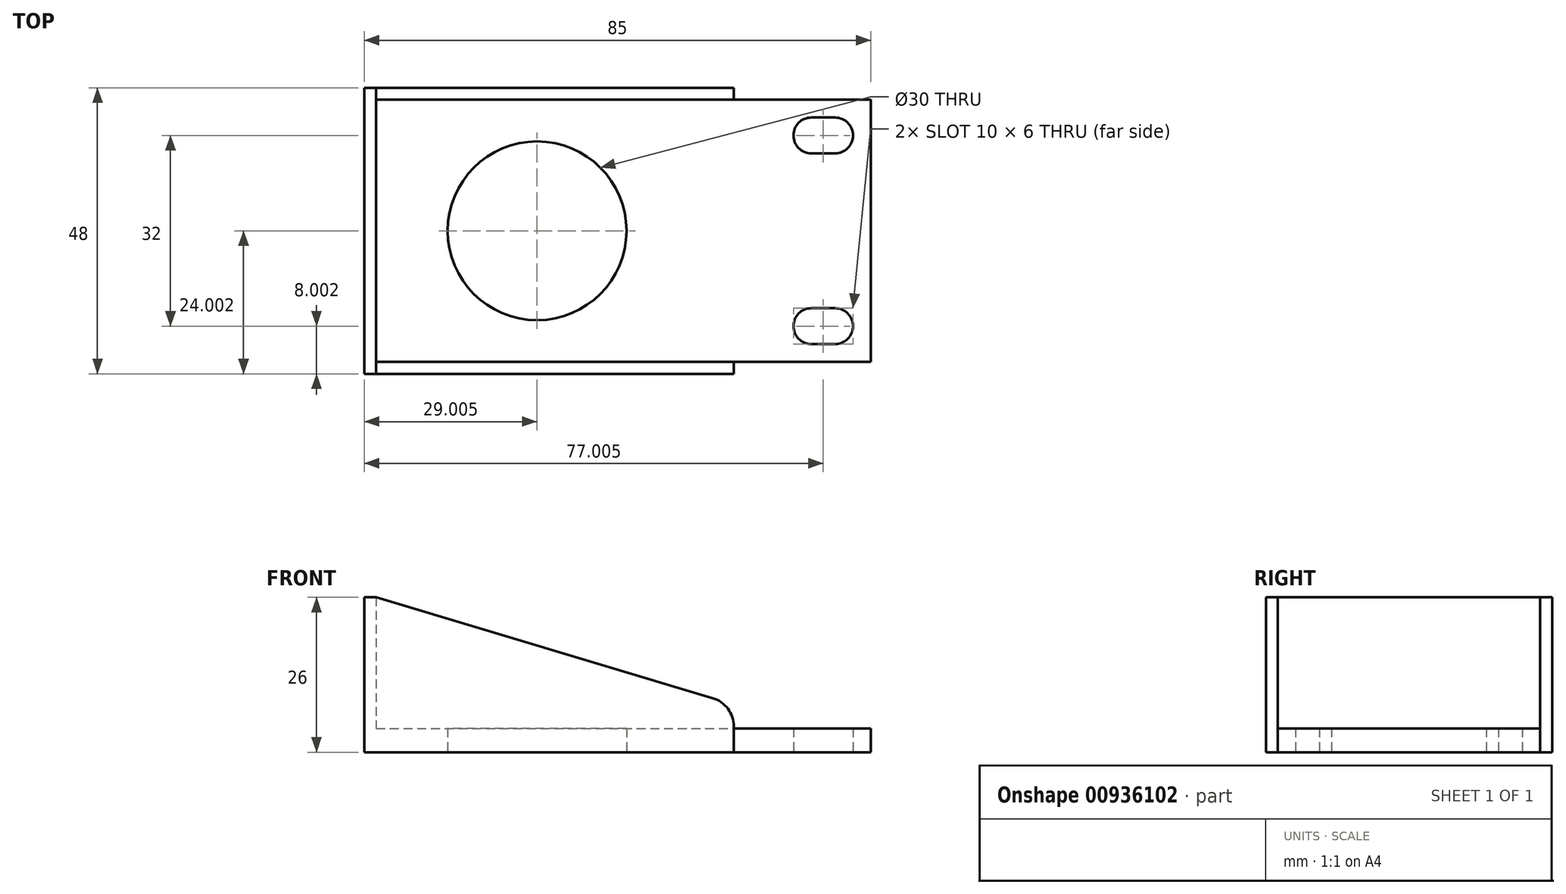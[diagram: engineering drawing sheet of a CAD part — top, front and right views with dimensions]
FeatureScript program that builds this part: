
annotation { "Feature Type Name" : "Feature", "Feature Type Description" : "" }
export const myFeature = defineFeature(function(context is Context, id is Id, definition is map)
    precondition{}
    {
        {
            var Q0;
            Q0=qCreatedBy(makeId("Top.planeOp"),FACE);
            var sketch = newSketch(context, id + "F0", { "sketchPlane" : qUnion([Q0])});
            skLineSegment(sketch, "E0.bottom", {"start": v(-33.04, 51.41) * mm, "end": v(43.96, 51.41) * mm});
            skLineSegment(sketch, "E0.top", {"start": v(-33.04, 7.41) * mm, "end": v(43.96, 7.41) * mm});
            skLineSegment(sketch, "E0.left", {"start": v(-33.04, 51.41) * mm, "end": v(-33.04, 7.41) * mm});
            skLineSegment(sketch, "E0.right", {"start": v(43.96, 51.41) * mm, "end": v(43.96, 7.41) * mm});
            skCircle(sketch, "E1", {"center": v(37.96, 13.41) * mm, "radius": 3 * mm});
            skCircle(sketch, "E2", {"center": v(37.96, 45.41) * mm, "radius": 3 * mm});
            skCircle(sketch, "E3", {"center": v(33.96, 45.41) * mm, "radius": 3 * mm});
            skCircle(sketch, "E4", {"center": v(33.96, 13.41) * mm, "radius": 3 * mm});
            skLineSegment(sketch, "E5", {"start": v(37.96, 48.41) * mm, "end": v(33.96, 48.41) * mm});
            skLineSegment(sketch, "E6", {"start": v(33.96, 42.41) * mm, "end": v(37.96, 42.41) * mm});
            skLineSegment(sketch, "E7", {"start": v(37.96, 10.41) * mm, "end": v(33.96, 10.41) * mm});
            skLineSegment(sketch, "E8", {"start": v(33.96, 16.41) * mm, "end": v(37.96, 16.41) * mm});
            skCircle(sketch, "E9", {"center": v(-12.04, 29.41) * mm, "radius": 15 * mm});
            skSolve(sketch);
        }
        {
            var Q0;
            Q0=makeQuery(id+"F0.imprint","IMPRINT",FACE,{"disambiguationData":[TD([[makeQuery(id+"F0.imprint","IMPRINT",EDGE,{"derivedFrom":sQuery(id+"F0.wireOp",EDGE,"E0.bottom")}),-1.0]])]});
            extrude(context, id + "F1", {"entities" : qUnion([Q0]), "depth" : 4 * mm, "offsetDistance" : 25 * mm});
        }
        {
            var Q0;
            Q0=makeQuery(id+"F1.opExtrude","CAP_FACE",FACE,{"disambiguationData":[OSD([sQuery(id+"F0.wireOp",EDGE,"E0.bottom"),sQuery(id+"F0.wireOp",EDGE,"E0.top"),sQuery(id+"F0.wireOp",EDGE,"E0.left"),sQuery(id+"F0.wireOp",EDGE,"E0.right"),sQuery(id+"F0.wireOp",EDGE,"E1"),sQuery(id+"F0.wireOp",EDGE,"E2"),sQuery(id+"F0.wireOp",EDGE,"E3"),sQuery(id+"F0.wireOp",EDGE,"E4"),sQuery(id+"F0.wireOp",EDGE,"E5"),sQuery(id+"F0.wireOp",EDGE,"E6"),sQuery(id+"F0.wireOp",EDGE,"E7"),sQuery(id+"F0.wireOp",EDGE,"E8"),sQuery(id+"F0.wireOp",EDGE,"E9")])],"isStart":false});
            var sketch = newSketch(context, id + "F2", { "sketchPlane" : qUnion([Q0])});
            skLineSegment(sketch, "E10.bottom", {"start": v(-33.04, 51.41) * mm, "end": v(20.96, 51.41) * mm});
            skLineSegment(sketch, "E10.top", {"start": v(-33.04, 53.41) * mm, "end": v(20.96, 53.41) * mm});
            skLineSegment(sketch, "E10.left", {"start": v(-33.04, 51.41) * mm, "end": v(-33.04, 53.41) * mm});
            skLineSegment(sketch, "E10.right", {"start": v(20.96, 51.41) * mm, "end": v(20.96, 53.41) * mm});
            skLineSegment(sketch, "E11.bottom", {"start": v(-33.04, 7.41) * mm, "end": v(20.96, 7.41) * mm});
            skLineSegment(sketch, "E11.top", {"start": v(-33.04, 5.41) * mm, "end": v(20.96, 5.41) * mm});
            skLineSegment(sketch, "E11.left", {"start": v(-33.04, 7.41) * mm, "end": v(-33.04, 5.41) * mm});
            skLineSegment(sketch, "E11.right", {"start": v(20.96, 7.41) * mm, "end": v(20.96, 5.41) * mm});
            skLineSegment(sketch, "E12.bottom", {"start": v(-33.04, 53.41) * mm, "end": v(-39.04, 53.41) * mm});
            skLineSegment(sketch, "E12.top", {"start": v(-33.04, 5.41) * mm, "end": v(-39.04, 5.41) * mm});
            skLineSegment(sketch, "E12.left", {"start": v(-33.04, 53.41) * mm, "end": v(-33.04, 5.41) * mm});
            skLineSegment(sketch, "E12.right", {"start": v(-39.04, 53.41) * mm, "end": v(-39.04, 5.41) * mm});
            skSolve(sketch);
        }
        {
            var Q0;
            {var subQ0=sQuery(id+"F2.wireOp",EDGE,"E10.bottom");Q0=makeQuery(id+"F2.imprint","IMPRINT",FACE,{"disambiguationData":[TD([[makeQuery(id+"F2.imprint","IMPRINT",EDGE,{"derivedFrom":subQ0}),1.0]])]});}
            var Q1;
            {var subQ3=sQuery(id+"F2.wireOp",EDGE,"E12.bottom");Q1=makeQuery(id+"F2.imprint","IMPRINT",FACE,{"disambiguationData":[TD([[makeQuery(id+"F2.imprint","IMPRINT",EDGE,{"derivedFrom":subQ3}),1.0]])]});}
            var Q2;
            {var subQ0=sQuery(id+"F2.wireOp",EDGE,"E11.bottom");Q2=makeQuery(id+"F2.imprint","IMPRINT",FACE,{"disambiguationData":[TD([[makeQuery(id+"F2.imprint","IMPRINT",EDGE,{"derivedFrom":subQ0}),-1.0]])]});}
            extrude(context, id + "F3", {"entities" : qUnion([Q0, Q1, Q2]), "depth" : -4 * mm, "offsetDistance" : 25 * mm});
        }
        {
            var Q0;
            Q0=makeQuery(id+"F3.opExtrude","CAP_FACE",FACE,{"disambiguationData":[OSD([sQuery(id+"F2.wireOp",EDGE,"E10.bottom"),sQuery(id+"F2.wireOp",EDGE,"E10.top"),sQuery(id+"F2.wireOp",EDGE,"E10.right"),sQuery(id+"F2.wireOp",EDGE,"E11.bottom"),sQuery(id+"F2.wireOp",EDGE,"E11.top"),sQuery(id+"F2.wireOp",EDGE,"E11.right"),sQuery(id+"F2.wireOp",EDGE,"E12.bottom"),sQuery(id+"F2.wireOp",EDGE,"E12.top"),sQuery(id+"F2.wireOp",EDGE,"E12.left"),sQuery(id+"F2.wireOp",EDGE,"E12.right")])],"isStart":true});
            var sketch = newSketch(context, id + "F4", { "sketchPlane" : qUnion([Q0])});
            skLineSegment(sketch, "E13.bottom", {"start": v(-39.04, 53.41) * mm, "end": v(-41.04, 53.41) * mm});
            skLineSegment(sketch, "E13.top", {"start": v(-39.04, 5.41) * mm, "end": v(-41.04, 5.41) * mm});
            skLineSegment(sketch, "E13.left", {"start": v(-39.04, 53.41) * mm, "end": v(-39.04, 5.41) * mm});
            skLineSegment(sketch, "E13.right", {"start": v(-41.04, 53.41) * mm, "end": v(-41.04, 5.41) * mm});
            skSolve(sketch);
        }
        {
            var Q0;
            Q0=makeQuery(id+"F4.imprint","IMPRINT",FACE,{"disambiguationData":[TD([[makeQuery(id+"F4.imprint","IMPRINT",EDGE,{"derivedFrom":sQuery(id+"F4.wireOp",EDGE,"E13.bottom")}),1.0]])]});
            extrude(context, id + "F5", {"entities" : qUnion([Q0]), "operationType" : NewBodyOperationType.ADD, "depth" : -4 * mm, "offsetDistance" : 25 * mm});
        }
        {
            var Q0;
            Q0=makeQuery(id+"F5.boolean.opBoolean","MERGE",FACE,{"derivedFrom":[makeQuery(id+"F3.opExtrude","CAP_FACE",FACE,{"disambiguationData":[OSD([sQuery(id+"F2.wireOp",EDGE,"E10.bottom"),sQuery(id+"F2.wireOp",EDGE,"E10.top"),sQuery(id+"F2.wireOp",EDGE,"E10.right"),sQuery(id+"F2.wireOp",EDGE,"E11.bottom"),sQuery(id+"F2.wireOp",EDGE,"E11.top"),sQuery(id+"F2.wireOp",EDGE,"E11.right"),sQuery(id+"F2.wireOp",EDGE,"E12.bottom"),sQuery(id+"F2.wireOp",EDGE,"E12.top"),sQuery(id+"F2.wireOp",EDGE,"E12.left"),sQuery(id+"F2.wireOp",EDGE,"E12.right")])],"isStart":true}),makeQuery(id+"F5.opExtrude","CAP_FACE",FACE,{"disambiguationData":[OSD([sQuery(id+"F4.wireOp",EDGE,"E13.bottom"),sQuery(id+"F4.wireOp",EDGE,"E13.top"),sQuery(id+"F4.wireOp",EDGE,"E13.left"),sQuery(id+"F4.wireOp",EDGE,"E13.right")])],"isStart":true})]});
            var sketch = newSketch(context, id + "F6", { "sketchPlane" : qUnion([Q0])});
            skLineSegment(sketch, "E14.bottom", {"start": v(-41.04, 53.41) * mm, "end": v(-39.04, 53.41) * mm});
            skLineSegment(sketch, "E14.top", {"start": v(-41.04, 5.41) * mm, "end": v(-39.04, 5.41) * mm});
            skLineSegment(sketch, "E14.left", {"start": v(-41.04, 53.41) * mm, "end": v(-41.04, 5.41) * mm});
            skLineSegment(sketch, "E14.right", {"start": v(-39.04, 53.41) * mm, "end": v(-39.04, 5.41) * mm});
            skSolve(sketch);
        }
        {
            var Q0;
            Q0=makeQuery(id+"F6.imprint","IMPRINT",FACE,{"disambiguationData":[TD([[makeQuery(id+"F6.imprint","IMPRINT",EDGE,{"derivedFrom":sQuery(id+"F6.wireOp",EDGE,"E14.bottom")}),-1.0]])]});
            extrude(context, id + "F7", {"entities" : qUnion([Q0]), "operationType" : NewBodyOperationType.ADD, "depth" : 22 * mm, "offsetDistance" : 25 * mm});
        }
        {
            var Q0;
            Q0=makeQuery(id+"F7.boolean.opBoolean","MERGE",FACE,{"derivedFrom":[makeQuery(id+"F5.boolean.opBoolean","MERGE",FACE,{"derivedFrom":[makeQuery(id+"F3.opExtrude","SWEPT_FACE",FACE,{"disambiguationData":[OSD([sQuery(id+"F2.wireOp",EDGE,"E11.top"),sQuery(id+"F2.wireOp",EDGE,"E12.top")])]}),makeQuery(id+"F5.opExtrude","SWEPT_FACE",FACE,{"disambiguationData":[OSD([sQuery(id+"F4.wireOp",EDGE,"E13.top")])]})]}),makeQuery(id+"F7.opExtrude","SWEPT_FACE",FACE,{"disambiguationData":[OSD([sQuery(id+"F6.wireOp",EDGE,"E14.top")])]})]});
            var sketch = newSketch(context, id + "F8", { "sketchPlane" : qUnion([Q0])});
            skLineSegment(sketch, "E15", {"start": v(20.96, 4) * mm, "end": v(20.96, 8) * mm});
            skLineSegment(sketch, "E16", {"start": v(20.96, 8) * mm, "end": v(-39.04, 26) * mm});
            skSolve(sketch);
        }
        {
            var Q0;
            Q0=makeQuery(id+"F8.imprint","IMPRINT",FACE,{"disambiguationData":[TD([[makeQuery(id+"F8.imprint","IMPRINT",EDGE,{"derivedFrom":sQuery(id+"F8.wireOp",EDGE,"E15")}),1.0]])]});
            extrude(context, id + "F9", {"entities" : qUnion([Q0]), "operationType" : NewBodyOperationType.ADD, "depth" : -2 * mm, "offsetDistance" : 25 * mm});
        }
        {
            var Q0;
            Q0=makeQuery(id+"F7.boolean.opBoolean","MERGE",FACE,{"derivedFrom":[makeQuery(id+"F5.boolean.opBoolean","MERGE",FACE,{"derivedFrom":[makeQuery(id+"F3.opExtrude","SWEPT_FACE",FACE,{"disambiguationData":[OSD([sQuery(id+"F2.wireOp",EDGE,"E10.top"),sQuery(id+"F2.wireOp",EDGE,"E12.bottom")])]}),makeQuery(id+"F5.opExtrude","SWEPT_FACE",FACE,{"disambiguationData":[OSD([sQuery(id+"F4.wireOp",EDGE,"E13.bottom")])]})]}),makeQuery(id+"F7.opExtrude","SWEPT_FACE",FACE,{"disambiguationData":[OSD([sQuery(id+"F6.wireOp",EDGE,"E14.bottom")])]})]});
            var sketch = newSketch(context, id + "F10", { "sketchPlane" : qUnion([Q0])});
            skLineSegment(sketch, "E17", {"start": v(-20.96, 4) * mm, "end": v(-20.96, 8) * mm});
            skLineSegment(sketch, "E18", {"start": v(-20.96, 8) * mm, "end": v(39.04, 26) * mm});
            skSolve(sketch);
        }
        {
            var Q0;
            Q0=makeQuery(id+"F10.imprint","IMPRINT",FACE,{"disambiguationData":[TD([[makeQuery(id+"F10.imprint","IMPRINT",EDGE,{"derivedFrom":sQuery(id+"F10.wireOp",EDGE,"E17")}),-1.0]])]});
            extrude(context, id + "F11", {"entities" : qUnion([Q0]), "operationType" : NewBodyOperationType.ADD, "depth" : -2 * mm, "offsetDistance" : 25 * mm});
        }
        {
            var Q0;
            Q0=makeQuery(id+"F11.opExtrude","SWEPT_EDGE",EDGE,{"disambiguationData":[OSD([sQuery(id+"F10.wireOp",EDGE,"E17"),sQuery(id+"F10.wireOp",EDGE,"E18")])]});
            fillet(context, id + "F12", {"entities" : qUnion([Q0]), "radius" : 5 * mm, "tangentPropagation" : true, "allowEdgeOverflow" : false});
        }
        {
            var Q0;
            Q0=makeQuery(id+"F9.opExtrude","SWEPT_EDGE",EDGE,{"disambiguationData":[OSD([sQuery(id+"F8.wireOp",EDGE,"E15"),sQuery(id+"F8.wireOp",EDGE,"E16")])]});
            fillet(context, id + "F13", {"entities" : qUnion([Q0]), "radius" : 5 * mm, "tangentPropagation" : true, "allowEdgeOverflow" : false});
        }
    });
